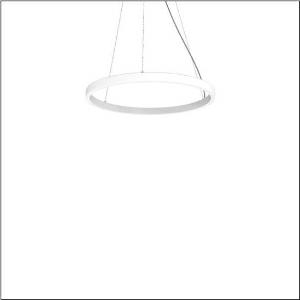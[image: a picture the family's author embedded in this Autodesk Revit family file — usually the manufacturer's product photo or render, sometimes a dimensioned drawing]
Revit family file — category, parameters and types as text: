
# Revit family: silica_r__21_ring-o_5pjbo2d1004a_430d
name_source: partatom
category: Lighting Fixtures
units: mm (PartAtom-declared; Revit-internal decimal feet)

## family parameters
Cut with Voids When Loaded = No
Host = Face
Light Source = No
Part Type = Normal
Room Calculation Point = No
Round Connector Dimension = Use Diameter
Shared = No

## types (1)
- Silica® 21 Ring-O (1 x LED, 4700 lm, 80 W, 3000K)
    Apparent Load = 80 VA
    CIE Flux Codes = 2 16 49 50 100
    Color Rendering = 80
    Color Temperature = 3000K
    Default Elevation = 1800 mm
    Description = Silica® 21 Ring-O, suspended luminaire, of PMMA, frosted, light emission: outer ring side luminous distribution, primary light characteristic: symmetric, installation type: suspended mounting, LED, rated luminous flux: 4.700lm, luminous efficacy: 59lm/W, light colour: 830, colour temperature: 3000K, control gear: DALI 2, with terminal, 5-pole, mains connection: 230V, AC/DC, 0/50..60Hz, rated input power: 80W, housing, of extruded aluminium section, traffic white (RAL 9016), diameter: 810mm, ceiling canopy, traffic white (RAL 9016), protection rating (lamp compartment): IP40, insulation class (complete): insulation class I (protective earthing), certification: CE, impact resistance: IK02, permissible operating ambient temperature: 0..+35°C, packaging unit: 1 piece
    Height = 48 mm  [stored 0.15748 ft]
    Lamp = 1 x LED
    Lamp Light Flux = 4700 lm
    Lamp Power = 80 W
    Lamp count = 1
    Length = 810 mm
    Luminous efficacy = 59 lm/W
    Manufacturer = Siteco
    ModVariant = No
    Model = 5PJBO2D1004A
    Mounting Place = Ceiling
    Mounting Type = Pendant
    Number of Poles = 1
    OnlyDefault = Yes
    Power Factor = 1
    Product Name = Silica® 21 Ring-O
    Product group = suspended luminaire
    ProductGroupID = 905
    Protection Class = Protection class I
    Protection Degree = IP 40
    RLX_Detail_Level = 1
    RLX_Emergency_Light_Flux = 0 lm
    RLX_Emergency_Type = 0
    RLX_Emergency_Type_DB = No
    RlxData = <blob elided: 12013 chars, md5=9cdf2052>
    Socket = socket
    Standby Power = 0 W
    System Light Flux = 4700 lm
    System Power = 80 W
    Type Comments = Product without accessories
    Type Image = l_1258383.jpg
    URL = http://relux.com
    VarID = ---
    Voltage = 0 V
    Weight = 0.00 kg
    Width = 0 mm  [stored 0 ft]

note: [stored X ft] marks values corroborated as IEEE doubles in the binary element streams (Revit-internal decimal feet)

## geometry (parser evidence)
native form markers: Sweep x12
no freeform markers — native parametric forms only
